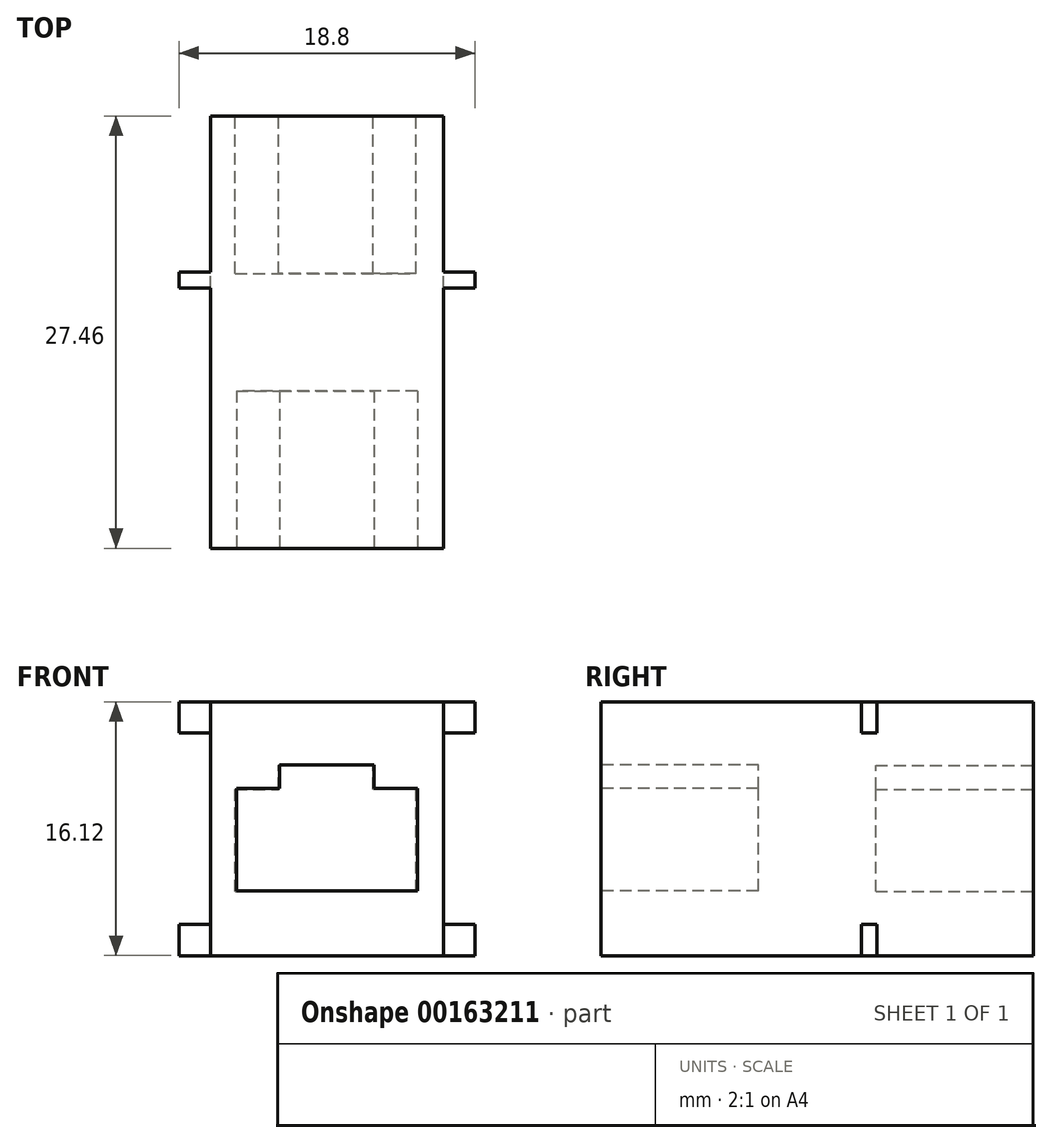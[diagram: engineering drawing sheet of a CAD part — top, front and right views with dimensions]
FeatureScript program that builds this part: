
annotation { "Feature Type Name" : "Feature", "Feature Type Description" : "" }
export const myFeature = defineFeature(function(context is Context, id is Id, definition is map)
    precondition{}
    {
        {
            var Q0;
            Q0=qCreatedBy(makeId("Front.planeOp"),FACE);
            var sketch = newSketch(context, id + "F0", { "sketchPlane" : qUnion([Q0])});
            skLineSegment(sketch, "E0.bottom", {"start": v(-7.4, 8.06) * mm, "end": v(7.4, 8.06) * mm});
            skLineSegment(sketch, "E0.top", {"start": v(-7.4, -8.06) * mm, "end": v(7.4, -8.06) * mm});
            skLineSegment(sketch, "E0.left", {"start": v(-7.4, 8.06) * mm, "end": v(-7.4, -8.06) * mm});
            skLineSegment(sketch, "E0.right", {"start": v(7.4, 8.06) * mm, "end": v(7.4, -8.06) * mm});
            skPoint(sketch, "E0.middle", {"position": v(0, 0) * mm});
            skLineSegment(sketch, "E1.bottom", {"start": v(-7.4, 8.06) * mm, "end": v(-9.4, 8.06) * mm});
            skLineSegment(sketch, "E1.top", {"start": v(-7.4, 6.07) * mm, "end": v(-9.4, 6.07) * mm});
            skLineSegment(sketch, "E1.left", {"start": v(-7.4, 8.06) * mm, "end": v(-7.4, 6.07) * mm});
            skLineSegment(sketch, "E1.right", {"start": v(-9.4, 8.06) * mm, "end": v(-9.4, 6.07) * mm});
            skLineSegment(sketch, "E2.bottom", {"start": v(-7.4, -8.06) * mm, "end": v(-9.4, -8.06) * mm});
            skLineSegment(sketch, "E2.top", {"start": v(-7.4, -6.06) * mm, "end": v(-9.4, -6.06) * mm});
            skLineSegment(sketch, "E2.left", {"start": v(-7.4, -8.06) * mm, "end": v(-7.4, -6.06) * mm});
            skLineSegment(sketch, "E2.right", {"start": v(-9.4, -8.06) * mm, "end": v(-9.4, -6.06) * mm});
            skPoint(sketch, "E3.oppositeSnap0", {"position": v(-8.4, -6.06) * mm});
            skLineSegment(sketch, "E3.bottom", {"start": v(7.4, -8.06) * mm, "end": v(9.4, -8.06) * mm});
            skLineSegment(sketch, "E3.top", {"start": v(7.4, -6.06) * mm, "end": v(9.4, -6.06) * mm});
            skLineSegment(sketch, "E3.left", {"start": v(7.4, -8.06) * mm, "end": v(7.4, -6.06) * mm});
            skLineSegment(sketch, "E3.right", {"start": v(9.4, -8.06) * mm, "end": v(9.4, -6.06) * mm});
            skLineSegment(sketch, "E4.bottom", {"start": v(7.4, 8.06) * mm, "end": v(9.4, 8.06) * mm});
            skLineSegment(sketch, "E4.top", {"start": v(7.4, 6.07) * mm, "end": v(9.4, 6.07) * mm});
            skLineSegment(sketch, "E4.left", {"start": v(7.4, 8.06) * mm, "end": v(7.4, 6.07) * mm});
            skLineSegment(sketch, "E4.right", {"start": v(9.4, 8.07) * mm, "end": v(9.4, 6.07) * mm});
            skSolve(sketch);
        }
        {
            var Q0;
            Q0=makeQuery(id+"F0.imprint","IMPRINT",FACE,{"disambiguationData":[TD([[makeQuery(id+"F0.imprint","IMPRINT",EDGE,{"derivedFrom":sQuery(id+"F0.wireOp",EDGE,"E0.bottom")}),-1.0]])]});
            extrude(context, id + "F1", {"entities" : qUnion([Q0]), "depth" : 17.54 * mm, "hasSecondDirection" : true, "secondDirectionOppositeDirection" : true, "secondDirectionDepth" : (27.46 - 17.54) * mm});
        }
        {
            var Q0;
            Q0=makeQuery(id+"F0.imprint","IMPRINT",FACE,{"disambiguationData":[TD([[makeQuery(id+"F0.imprint","IMPRINT",EDGE,{"derivedFrom":sQuery(id+"F0.wireOp",EDGE,"E1.bottom")}),1.0]])]});
            var Q1;
            Q1=makeQuery(id+"F0.imprint","IMPRINT",FACE,{"disambiguationData":[TD([[makeQuery(id+"F0.imprint","IMPRINT",EDGE,{"derivedFrom":sQuery(id+"F0.wireOp",EDGE,"E2.bottom")}),-1.0]])]});
            var Q2;
            Q2=makeQuery(id+"F0.imprint","IMPRINT",FACE,{"disambiguationData":[TD([[makeQuery(id+"F0.imprint","IMPRINT",EDGE,{"derivedFrom":sQuery(id+"F0.wireOp",EDGE,"E3.bottom")}),1.0]])]});
            var Q3;
            Q3=makeQuery(id+"F0.imprint","IMPRINT",FACE,{"disambiguationData":[TD([[makeQuery(id+"F0.imprint","IMPRINT",EDGE,{"derivedFrom":sQuery(id+"F0.wireOp",EDGE,"E4.bottom")}),-1.0]])]});
            extrude(context, id + "F2", {"entities" : qUnion([Q0, Q1, Q2, Q3]), "operationType" : NewBodyOperationType.ADD, "depth" : 1 * mm});
        }
        {
            var Q0;
            Q0=makeQuery(id+"F1.opExtrude","CAP_FACE",FACE,{"disambiguationData":[OSD([sQuery(id+"F0.wireOp",EDGE,"E0.bottom"),sQuery(id+"F0.wireOp",EDGE,"E0.top"),sQuery(id+"F0.wireOp",EDGE,"E0.left"),sQuery(id+"F0.wireOp",EDGE,"E0.right"),sQuery(id+"F0.wireOp",EDGE,"E1.left"),sQuery(id+"F0.wireOp",EDGE,"E2.left"),sQuery(id+"F0.wireOp",EDGE,"E3.left"),sQuery(id+"F0.wireOp",EDGE,"E4.left")])],"isStart":false});
            var sketch = newSketch(context, id + "F3", { "sketchPlane" : qUnion([Q0])});
            skLineSegment(sketch, "E5", {"start": v(0, -3.95) * mm, "end": v(-5.75, -3.95) * mm});
            skLineSegment(sketch, "E6", {"start": v(-5.75, -3.95) * mm, "end": v(-5.75, 2.55) * mm});
            skLineSegment(sketch, "E7", {"start": v(-5.75, 2.55) * mm, "end": v(-3, 2.55) * mm});
            skLineSegment(sketch, "E8", {"start": v(-3, 2.55) * mm, "end": v(-3, 4.05) * mm});
            skLineSegment(sketch, "E9", {"start": v(0, 4.05) * mm, "end": v(-3, 4.05) * mm});
            skLineSegment(sketch, "E10.MirrorCS", {"start": v(3, 2.55) * mm, "end": v(3, 4.05) * mm});
            skLineSegment(sketch, "E11.MirrorCS", {"start": v(0, 4.05) * mm, "end": v(3, 4.05) * mm});
            skLineSegment(sketch, "E12.MirrorCS", {"start": v(0, -3.95) * mm, "end": v(5.75, -3.95) * mm});
            skLineSegment(sketch, "E13.MirrorCS", {"start": v(5.75, -3.95) * mm, "end": v(5.75, 2.55) * mm});
            skLineSegment(sketch, "E14.MirrorCS", {"start": v(5.75, 2.55) * mm, "end": v(3, 2.55) * mm});
            skSolve(sketch);
        }
        {
            var Q0;
            Q0=makeQuery(id+"F3.imprint","IMPRINT",FACE,{"disambiguationData":[TD([[makeQuery(id+"F3.imprint","IMPRINT",EDGE,{"derivedFrom":sQuery(id+"F3.wireOp",EDGE,"E5")}),-1.0]])]});
            extrude(context, id + "F4", {"entities" : qUnion([Q0]), "operationType" : NewBodyOperationType.REMOVE, "oppositeDirection" : true, "depth" : 10 * mm});
        }
        {
            var Q0;
            Q0=makeQuery(id+"F1.opExtrude","CAP_FACE",FACE,{"disambiguationData":[OSD([sQuery(id+"F0.wireOp",EDGE,"E0.bottom"),sQuery(id+"F0.wireOp",EDGE,"E0.top"),sQuery(id+"F0.wireOp",EDGE,"E0.left"),sQuery(id+"F0.wireOp",EDGE,"E0.right"),sQuery(id+"F0.wireOp",EDGE,"E1.left"),sQuery(id+"F0.wireOp",EDGE,"E2.left"),sQuery(id+"F0.wireOp",EDGE,"E3.left"),sQuery(id+"F0.wireOp",EDGE,"E4.left")])],"isStart":true});
            var sketch = newSketch(context, id + "F5", { "sketchPlane" : qUnion([Q0])});
            skLineSegment(sketch, "E15", {"start": v(0.08, -4) * mm, "end": v(-5.67, -4) * mm});
            skLineSegment(sketch, "E16", {"start": v(-5.67, -4) * mm, "end": v(-5.67, 2.5) * mm});
            skLineSegment(sketch, "E17", {"start": v(-5.67, 2.5) * mm, "end": v(-2.92, 2.5) * mm});
            skLineSegment(sketch, "E18", {"start": v(-2.92, 2.5) * mm, "end": v(-2.92, 4) * mm});
            skLineSegment(sketch, "E19", {"start": v(0.08, 4) * mm, "end": v(-2.92, 4) * mm});
            skLineSegment(sketch, "E20.MirrorCS", {"start": v(3.08, 2.5) * mm, "end": v(3.08, 4) * mm});
            skLineSegment(sketch, "E21.MirrorCS", {"start": v(0.08, 4) * mm, "end": v(3.08, 4) * mm});
            skLineSegment(sketch, "E22.MirrorCS", {"start": v(0.08, -4) * mm, "end": v(5.83, -4) * mm});
            skLineSegment(sketch, "E23.MirrorCS", {"start": v(5.83, -4) * mm, "end": v(5.83, 2.5) * mm});
            skLineSegment(sketch, "E24.MirrorCS", {"start": v(5.83, 2.5) * mm, "end": v(3.08, 2.5) * mm});
            skSolve(sketch);
        }
        {
            var Q0;
            Q0=makeQuery(id+"F5.imprint","IMPRINT",FACE,{"disambiguationData":[TD([[makeQuery(id+"F5.imprint","IMPRINT",EDGE,{"derivedFrom":sQuery(id+"F5.wireOp",EDGE,"E15")}),-1.0]])]});
            extrude(context, id + "F6", {"entities" : qUnion([Q0]), "operationType" : NewBodyOperationType.REMOVE, "oppositeDirection" : true, "depth" : 10 * mm});
        }
    });
